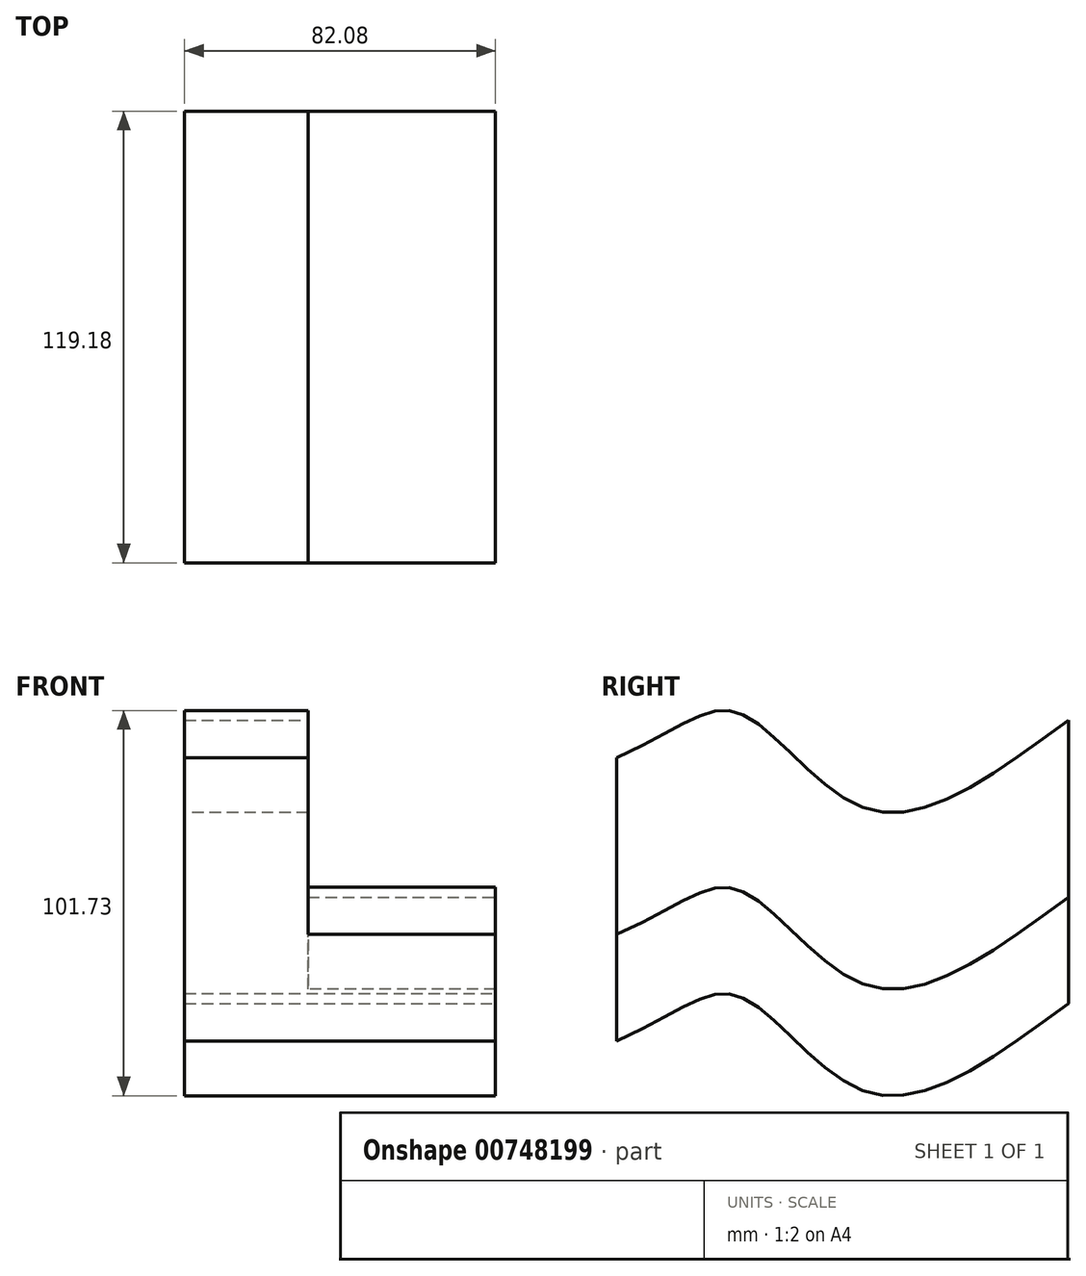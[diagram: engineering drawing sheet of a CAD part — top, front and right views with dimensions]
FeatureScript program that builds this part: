
annotation { "Feature Type Name" : "Feature", "Feature Type Description" : "" }
export const myFeature = defineFeature(function(context is Context, id is Id, definition is map)
    precondition{}
    {
        {
            var Q0;
            Q0=qCreatedBy(makeId("Front.planeOp"),FACE);
            var sketch = newSketch(context, id + "F0", { "sketchPlane" : qUnion([Q0])});
            skLineSegment(sketch, "E0.bottom", {"start": v(-59.3, 28.25) * mm, "end": v(-26.7, 28.25) * mm});
            skLineSegment(sketch, "E0.top", {"start": v(-59.3, -46.52) * mm, "end": v(-26.7, -46.52) * mm});
            skLineSegment(sketch, "E0.left", {"start": v(-59.3, 28.25) * mm, "end": v(-59.3, -46.52) * mm});
            skLineSegment(sketch, "E0.right", {"start": v(-26.7, 28.25) * mm, "end": v(-26.7, -18.41) * mm});
            skLineSegment(sketch, "E1.bottom", {"start": v(-26.7, -18.41) * mm, "end": v(22.77, -18.41) * mm});
            skLineSegment(sketch, "E1.top", {"start": v(-26.7, -46.52) * mm, "end": v(22.77, -46.52) * mm});
            skLineSegment(sketch, "E1.right", {"start": v(22.77, -18.41) * mm, "end": v(22.77, -46.52) * mm});
            skSolve(sketch);
        }
        {
            var Q0;
            Q0=qCreatedBy(makeId("Right.planeOp"),FACE);
            var sketch = newSketch(context, id + "F1", { "sketchPlane" : qUnion([Q0])});
            skFitSpline(sketch, "E2", {"points": [v(119.18, 36.68) * mm, v(66.05, 13.35) * mm, v(32.52, 38.49) * mm, v(0, 26.84) * mm], "startDerivative": vector(-158.72, -115.78) * mm, "endDerivative": vector(-168.85, -74.16) * mm});
            skSolve(sketch);
        }
        {
            var Q0;
            Q0=makeQuery(id+"F0.imprint","IMPRINT",FACE,{"disambiguationData":[TD([[makeQuery(id+"F0.imprint","IMPRINT",EDGE,{"derivedFrom":sQuery(id+"F0.wireOp",EDGE,"E0.bottom")}),-1.0]])]});
            var Q1;
            Q1=sQuery(id+"F1.wireOp",EDGE,"E2");
            sweep(context, id + "F2", {"profiles" : qUnion([Q0]), "path" : qUnion([Q1]), "keepProfileOrientation" : true});
        }
    });
